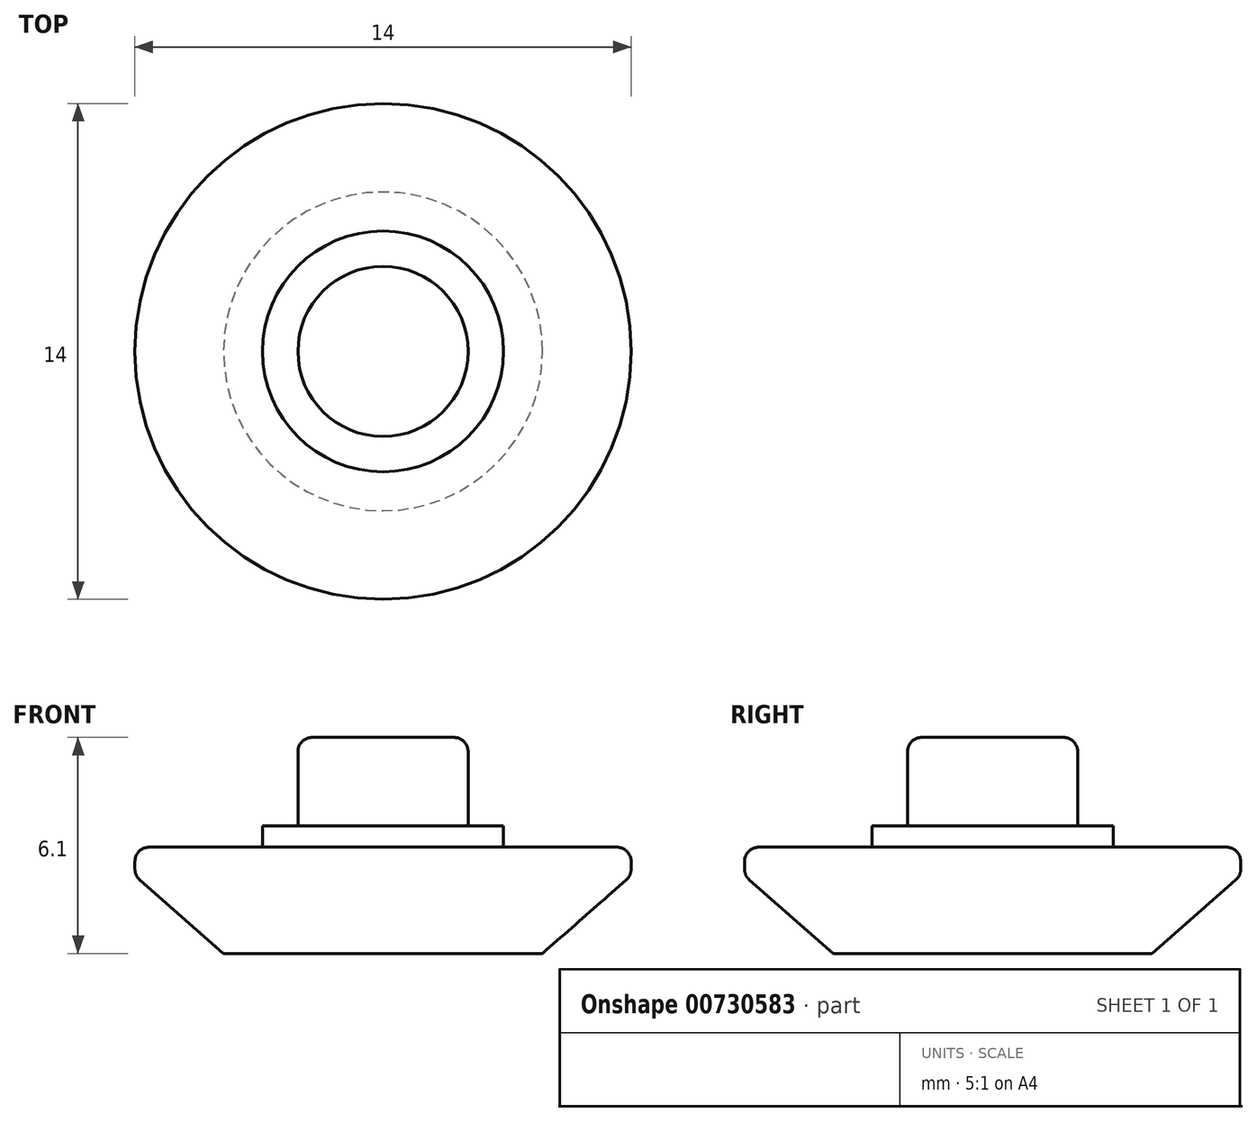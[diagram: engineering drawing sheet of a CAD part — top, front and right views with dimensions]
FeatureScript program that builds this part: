
annotation { "Feature Type Name" : "Feature", "Feature Type Description" : "" }
export const myFeature = defineFeature(function(context is Context, id is Id, definition is map)
    precondition{}
    {
        {
            var Q0;
            Q0=qCreatedBy(makeId("Front.planeOp"),FACE);
            var sketch = newSketch(context, id + "F0", { "sketchPlane" : qUnion([Q0])});
            skLineSegment(sketch, "E0", {"start": v(0, 0) * mm, "end": v(4.5, 0) * mm});
            skLineSegment(sketch, "E1", {"start": v(4.5, 0) * mm, "end": v(7, 2.2) * mm});
            skLineSegment(sketch, "E2", {"start": v(7, 2.2) * mm, "end": v(7, 3) * mm});
            skLineSegment(sketch, "E3", {"start": v(7, 3) * mm, "end": v(3.4, 3) * mm});
            skLineSegment(sketch, "E4", {"start": v(3.4, 3) * mm, "end": v(3.4, 3.6) * mm});
            skLineSegment(sketch, "E5", {"start": v(3.4, 3.6) * mm, "end": v(2.4, 3.6) * mm});
            skLineSegment(sketch, "E6", {"start": v(2.4, 3.6) * mm, "end": v(2.4, 6.1) * mm});
            skLineSegment(sketch, "E7", {"start": v(2.4, 6.1) * mm, "end": v(0, 6.1) * mm});
            skLineSegment(sketch, "E8", {"start": v(0, 6.1) * mm, "end": v(0, 0) * mm});
            skSolve(sketch);
        }
        {
            var Q0;
            Q0=qCreatedBy(makeId("Front.planeOp"),FACE);
            var sketch = newSketch(context, id + "F1", { "sketchPlane" : qUnion([Q0])});
            skLineSegment(sketch, "E9", {"start": v(0, 23.2) * mm, "end": v(0, 0) * mm, "construction": true});
            skSolve(sketch);
        }
        {
            var Q0;
            Q0 = qSketchRegion(id + "F0", true);
            var Q1;
            Q1=sQuery(id+"F1.wireOp",EDGE,"E9");
            revolve(context, id + "F2", {"surfaceOperationType" : NewSurfaceOperationType.NEW, "entities" : qUnion([Q0]), "axis" : qUnion([Q1]), "revolveType" : RevolveType.FULL});
        }
        {
            var Q0;
            Q0=makeQuery(id+"F2.opRevolve","SWEPT_EDGE",EDGE,{"disambiguationData":[OSD([sQuery(id+"F0.wireOp",EDGE,"E1"),sQuery(id+"F0.wireOp",EDGE,"E2")])]});
            var Q1;
            Q1=makeQuery(id+"F2.opRevolve","SWEPT_EDGE",EDGE,{"disambiguationData":[OSD([sQuery(id+"F0.wireOp",EDGE,"E6"),sQuery(id+"F0.wireOp",EDGE,"E7")])]});
            var Q2;
            Q2=makeQuery(id+"F2.opRevolve","SWEPT_EDGE",EDGE,{"disambiguationData":[OSD([sQuery(id+"F0.wireOp",EDGE,"E2"),sQuery(id+"F0.wireOp",EDGE,"E3")])]});
            fillet(context, id + "F3", {"entities" : qUnion([Q0, Q1, Q2]), "radius" : 0.4 * mm, "tangentPropagation" : true, "allowEdgeOverflow" : false});
        }
    });
